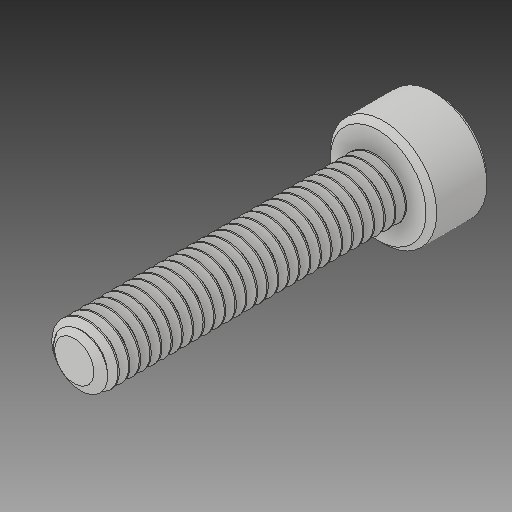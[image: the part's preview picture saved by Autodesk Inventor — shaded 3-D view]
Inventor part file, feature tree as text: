
AUTODESK INVENTOR PART (.ipt)
format: ipt  version: 2019.4 (Build 234330000, 330)  size: 923,136 bytes
history: native  units: in
note: dims shown in document units (in); Inventor stores cm internally (conversion verified against a paired STEP export)
features: chamfer x1
ambient origin geometry x8: Origin, YZ Plane, XZ Plane, XY Plane, X Axis, Y Axis, Z Axis, Center Point
bodies: Solid1 (feature_tree)
feature tree (1):
  chamfer  "Chamfer1"  [1 undecoded]
note: 1 required parameter value undecoded (feature->parameter linkage not recoverable at this tier; creation-order binding heuristic only, values carry confidence <= 0.55)
